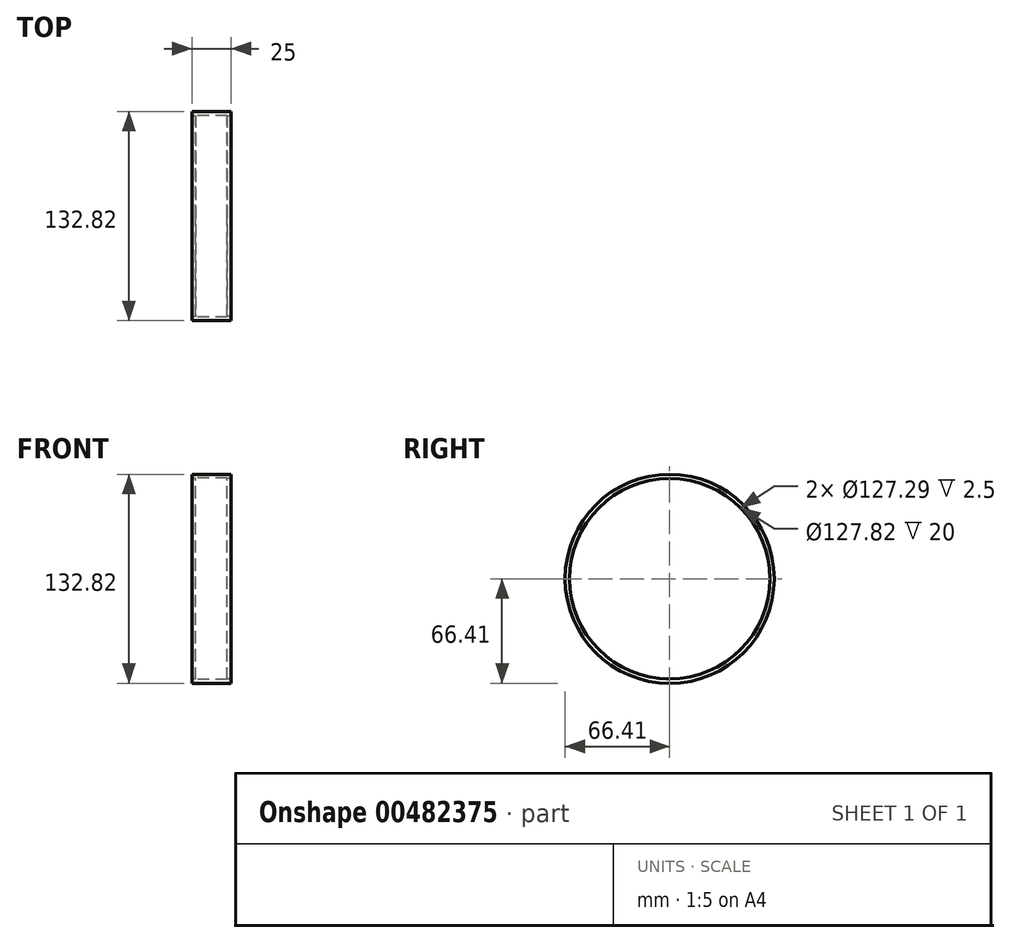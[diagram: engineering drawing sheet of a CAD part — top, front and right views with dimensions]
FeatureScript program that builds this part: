
annotation { "Feature Type Name" : "Feature", "Feature Type Description" : "" }
export const myFeature = defineFeature(function(context is Context, id is Id, definition is map)
    precondition{}
    {
        {
            var Q0;
            Q0=qCreatedBy(makeId("Right.planeOp"),FACE);
            var sketch = newSketch(context, id + "F0", { "sketchPlane" : qUnion([Q0])});
            skCircle(sketch, "E0", {"center": v(0, 0) * mm, "radius": 66.4 * mm});
            skCircle(sketch, "E1", {"center": v(0, 0) * mm, "radius": 63.65 * mm});
            skCircle(sketch, "E2", {"center": v(0, 0) * mm, "radius": 2.51 * mm});
            skSolve(sketch);
        }
        {
            var Q0;
            Q0 = qSketchRegion(id + "F0", true);
            extrude(context, id + "F1", {"entities" : qUnion([Q0]), "depth" : 25 * mm});
        }
        {
            var Q0;
            Q0=makeQuery(id+"F1.opExtrude","SWEPT_FACE",FACE,{"disambiguationData":[OSD([sQuery(id+"F0.wireOp",EDGE,"E1")])]});
            shell(context, id + "F2", {"entities" : qUnion([Q0]), "thickness" : 2.5 * mm});
        }
    });
